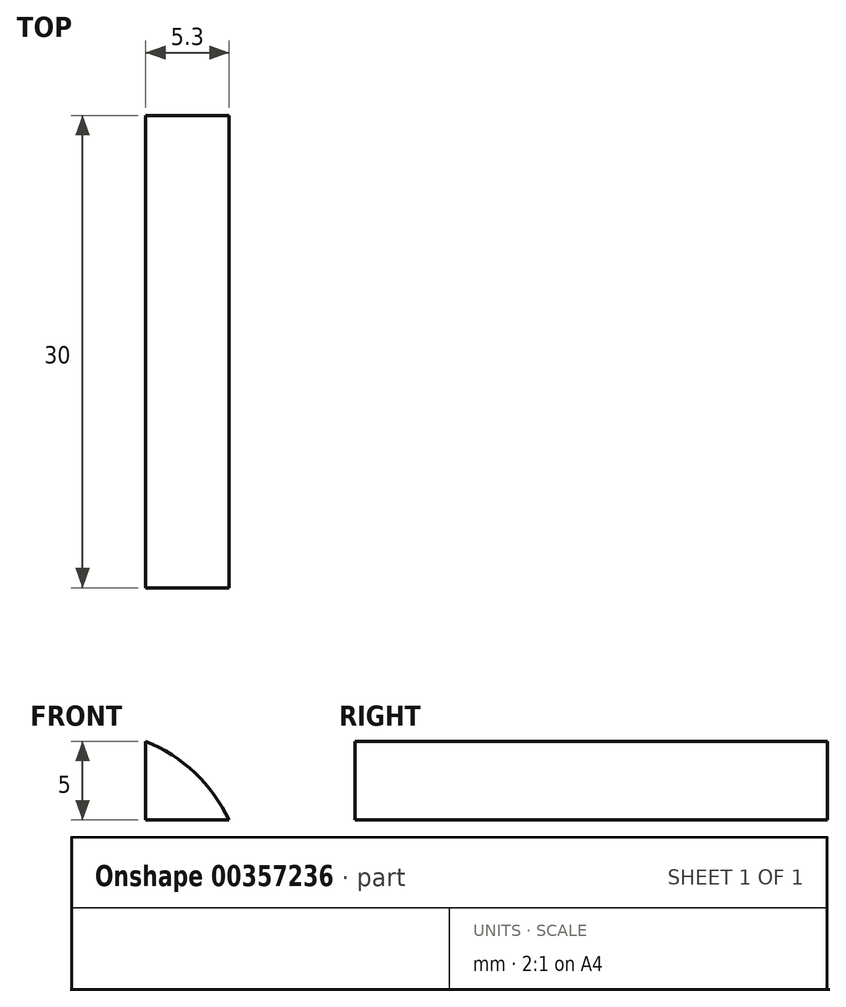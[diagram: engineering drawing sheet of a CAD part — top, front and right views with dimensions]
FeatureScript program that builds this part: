
annotation { "Feature Type Name" : "Feature", "Feature Type Description" : "" }
export const myFeature = defineFeature(function(context is Context, id is Id, definition is map)
    precondition{}
    {
        {
            var Q0;
            Q0=qCreatedBy(makeId("Top.planeOp"),FACE);
            var sketch = newSketch(context, id + "F0", { "sketchPlane" : qUnion([Q0])});
            skLineSegment(sketch, "E0.bottom", {"start": v(3.12, -15) * mm, "end": v(-3.13, -15) * mm});
            skLineSegment(sketch, "E0.top", {"start": v(3.13, 15) * mm, "end": v(-3.12, 15) * mm});
            skLineSegment(sketch, "E0.left", {"start": v(3.12, -15) * mm, "end": v(3.13, 15) * mm});
            skLineSegment(sketch, "E0.right", {"start": v(-3.13, -15) * mm, "end": v(-3.12, 15) * mm});
            skPoint(sketch, "E0.middle", {"position": v(0, 0) * mm});
            skSolve(sketch);
        }
        {
            var Q0;
            Q0 = qSketchRegion(id + "F0", true);
            extrude(context, id + "F1", {"entities" : qUnion([Q0]), "depth" : 5 * mm});
        }
        {
            var Q0;
            Q0=makeQuery(id+"F1.opExtrude","CAP_EDGE",EDGE,{"disambiguationData":[OSD([sQuery(id+"F0.wireOp",EDGE,"E0.left")])],"isStart":false});
            fillet(context, id + "F2", {"entities" : qUnion([Q0]), "radius" : 10 * mm, "tangentPropagation" : true, "allowEdgeOverflow" : false});
        }
    });
